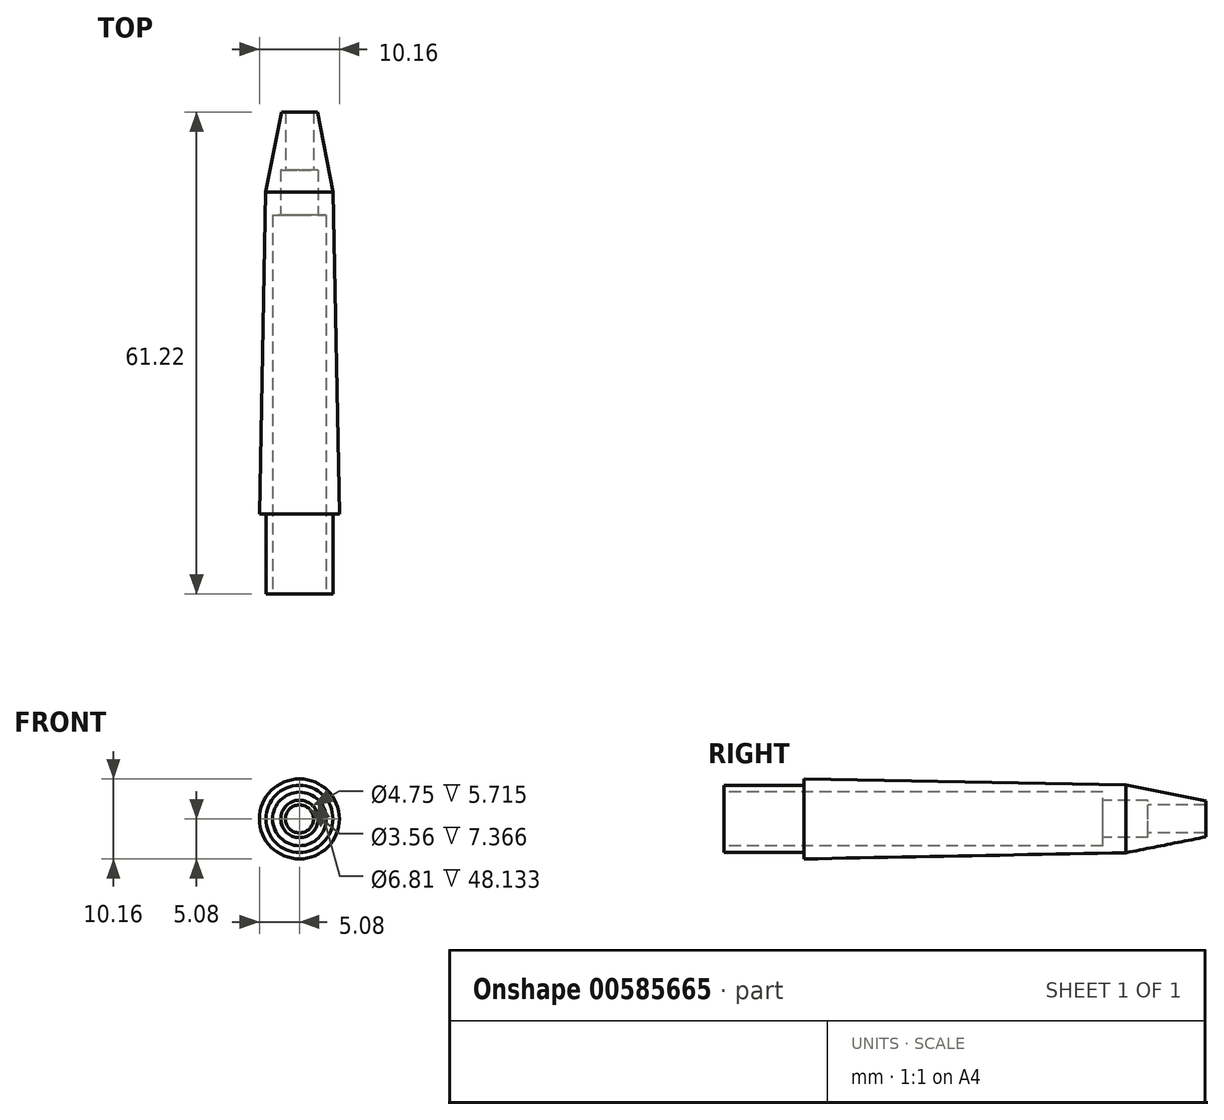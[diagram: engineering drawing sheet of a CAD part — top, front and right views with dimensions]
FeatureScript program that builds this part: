
annotation { "Feature Type Name" : "Feature", "Feature Type Description" : "" }
export const myFeature = defineFeature(function(context is Context, id is Id, definition is map)
    precondition{}
    {
        {
            var Q0;
            Q0=qCreatedBy(makeId("Right.planeOp"),FACE);
            var sketch = newSketch(context, id + "F0", { "sketchPlane" : qUnion([Q0])});
            skLineSegment(sketch, "E0", {"start": v(25.12, 3.4) * mm, "end": v(63.1, 3.4) * mm});
            skLineSegment(sketch, "E1", {"start": v(63.1, 3.4) * mm, "end": v(63.1, 2.37) * mm});
            skLineSegment(sketch, "E2", {"start": v(-4.62, 0) * mm, "end": v(19.03, 0) * mm});
            skLineSegment(sketch, "E3", {"start": v(76.18, 2.29) * mm, "end": v(76.18, 1.78) * mm});
            skLineSegment(sketch, "E4", {"start": v(76.18, 2.29) * mm, "end": v(66.02, 4.3) * mm});
            skLineSegment(sketch, "E5", {"start": v(63.1, 2.37) * mm, "end": v(68.81, 2.37) * mm});
            skLineSegment(sketch, "E6", {"start": v(76.18, 1.78) * mm, "end": v(68.81, 1.78) * mm});
            skLineSegment(sketch, "E7", {"start": v(68.81, 1.78) * mm, "end": v(68.81, 2.37) * mm});
            skLineSegment(sketch, "E8", {"start": v(25.12, 5.08) * mm, "end": v(66.02, 4.3) * mm});
            skLineSegment(sketch, "E9", {"start": v(25.12, 5.08) * mm, "end": v(25.12, 4.25) * mm});
            skLineSegment(sketch, "E10", {"start": v(25.12, 4.25) * mm, "end": v(14.96, 4.25) * mm});
            skLineSegment(sketch, "E11", {"start": v(14.96, 4.25) * mm, "end": v(14.96, 3.4) * mm});
            skLineSegment(sketch, "E12", {"start": v(14.96, 3.4) * mm, "end": v(25.12, 3.4) * mm});
            skSolve(sketch);
        }
        {
            var Q0;
            Q0 = qSketchRegion(id + "F0", true);
            var Q1;
            Q1=sQuery(id+"F0.wireOp",EDGE,"E2");
            revolve(context, id + "F1", {"entities" : qUnion([Q0]), "axis" : qUnion([Q1]), "revolveType" : RevolveType.FULL});
        }
    });
